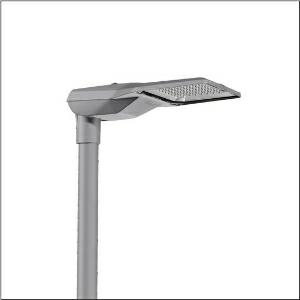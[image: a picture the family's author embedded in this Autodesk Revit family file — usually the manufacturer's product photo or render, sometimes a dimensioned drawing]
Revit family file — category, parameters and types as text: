
# Revit family: streetlight_sl_21_midi___p0_5a_5xe3v33s08mb_c878
name_source: partatom
category: Lighting Fixtures
units: mm (PartAtom-declared; Revit-internal decimal feet)

## family parameters
Cut with Voids When Loaded = No
Host = Face
Light Source = No
Part Type = Normal
Room Calculation Point = No
Round Connector Dimension = Use Diameter
Shared = No

## types (1)
- --- (1 x LED, 17960 lm, 136 W, 3000K)
    Apparent Load = 136 VA
    CIE Flux Codes = 37 73 96 100 100
    Color Rendering = 70
    Color Temperature = 3000K
    Default Elevation = 1800 mm
    Description = Streetlight SL 21 midi, mast luminaire, primary light control with lens, of PMMA, primary optical cover: cover, of toughened safety glass, transparent, light distribution: P0.5a, light emission: direct distribution, primary light characteristic: asymmetric, installation type: post-top, side-entry, LED, High Power LED, rated luminous flux: 17.960lm, luminous efficacy: 132lm/W, light colour: 730, colour temperature: 3000K, control gear: D4i, control: pre-setting: logarithmic dimming characteristic, flexible luminous flux parameterisation, time-dependent luminous flux control, constant luminous flux control, overheat protection, mains connection: 230..240V, AC, 50/60Hz, start of lifetime: 136W, end of service life: 142W, reduction: 61W, luminaire housing, of diecast aluminium, powder-coated, Siteco® metallic grey (DB 702S), corrosivity category C5 mid according to DIN EN ISO 12944, multi-level sealing system, sealing non-destructively replaceable, inclination adjustable: 0°, 5°, 10°, 15°, please order mast flange separately, length: 644mm, width: 335mm, height: 110mm, mast flange for spigot size: 42mm (side-entry): 5XC10008XM4, 60/48mm (side-entry/post-top): 5XC10108XM2, 76/60mm (side-entry/post-top): 5XC10108XM1, mounting height: 4..8m, Smart Interface above, protection rating (complete): IP66, insulation class (complete): insulation class II (safety insulation), certification: CE, ENEC, ENEC+, VDE, impact resistance: IK10, permissible operating ambient temperature for outdoor applications: -40..+50°C, standard-compliant lighting for roads and squares, packaging unit: 1 piece

Light Distribution: P0.5a
    Height = 111 mm
    Lamp = 1 x LED
    Lamp Light Flux = 17960 lm
    Lamp Power = 136 W
    Lamp count = 1
    Length = 644 mm
    Luminous efficacy = 132 lm/W
    Manufacturer = Siteco
    ModVariant = No
    Model = 5XE3V33S08MB
    Number of Poles = 1
    OnlyDefault = Yes
    Power Factor = 1
    Product Name = Streetlight SL 21 midi | P0.5a
    Product group = mast luminaire | pylon top
    ProductGroupID = 6100
    Protection Class = Protection class II
    Protection Degree = IP 66
    RLX_Detail_Level = 1
    RLX_Emergency_Light_Flux = 0 lm
    RLX_Emergency_Type = 0
    RLX_Emergency_Type_DB = No
    RlxData = <blob elided: 26369 chars, md5=3af12eef>
    Socket = socket
    Standby Power = 0 W
    System Light Flux = 17960 lm
    System Power = 136 W
    Type Comments = factory setting: luminous flux: 100 % | dim-lin: 254 | 695 mA
    Type Image = l_1004302.jpg
    URL = http://relux.com
    VarID = @adj_069914
    Voltage = 0 V
    Weight = 0.00 kg
    Width = 336 mm

## geometry (parser evidence)
native form markers: Blend x4, Sweep x12
no freeform markers — native parametric forms only
